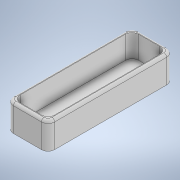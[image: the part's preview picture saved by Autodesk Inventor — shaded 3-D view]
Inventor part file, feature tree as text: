
AUTODESK INVENTOR PART (.ipt)
format: ipt  version: 2022 (Build 260153000, 153)  size: 158,208 bytes
history: native  units: mm
features: sketch x3, extrude x3, chamfer x1, fillet x1
ambient origin geometry x8: Origin, YZ Plane, XZ Plane, XY Plane, X Axis, Y Axis, Z Axis, Center Point
bodies: Solide1 (feature_tree)
feature tree (8):
  sketch  "Esquisse1"
  sketch  "Esquisse2"
  extrude  "Extrusion1"  Depth=31.0mm
  sketch  "Esquisse3"
  extrude  "Extrusion2"  Depth=94.0mm
  extrude  "Extrusion3"  Depth=5.0mm
  chamfer  "Chanfrein1"  Distance=20.0mm
  fillet  "Congé1"  Radius=26.0mm
